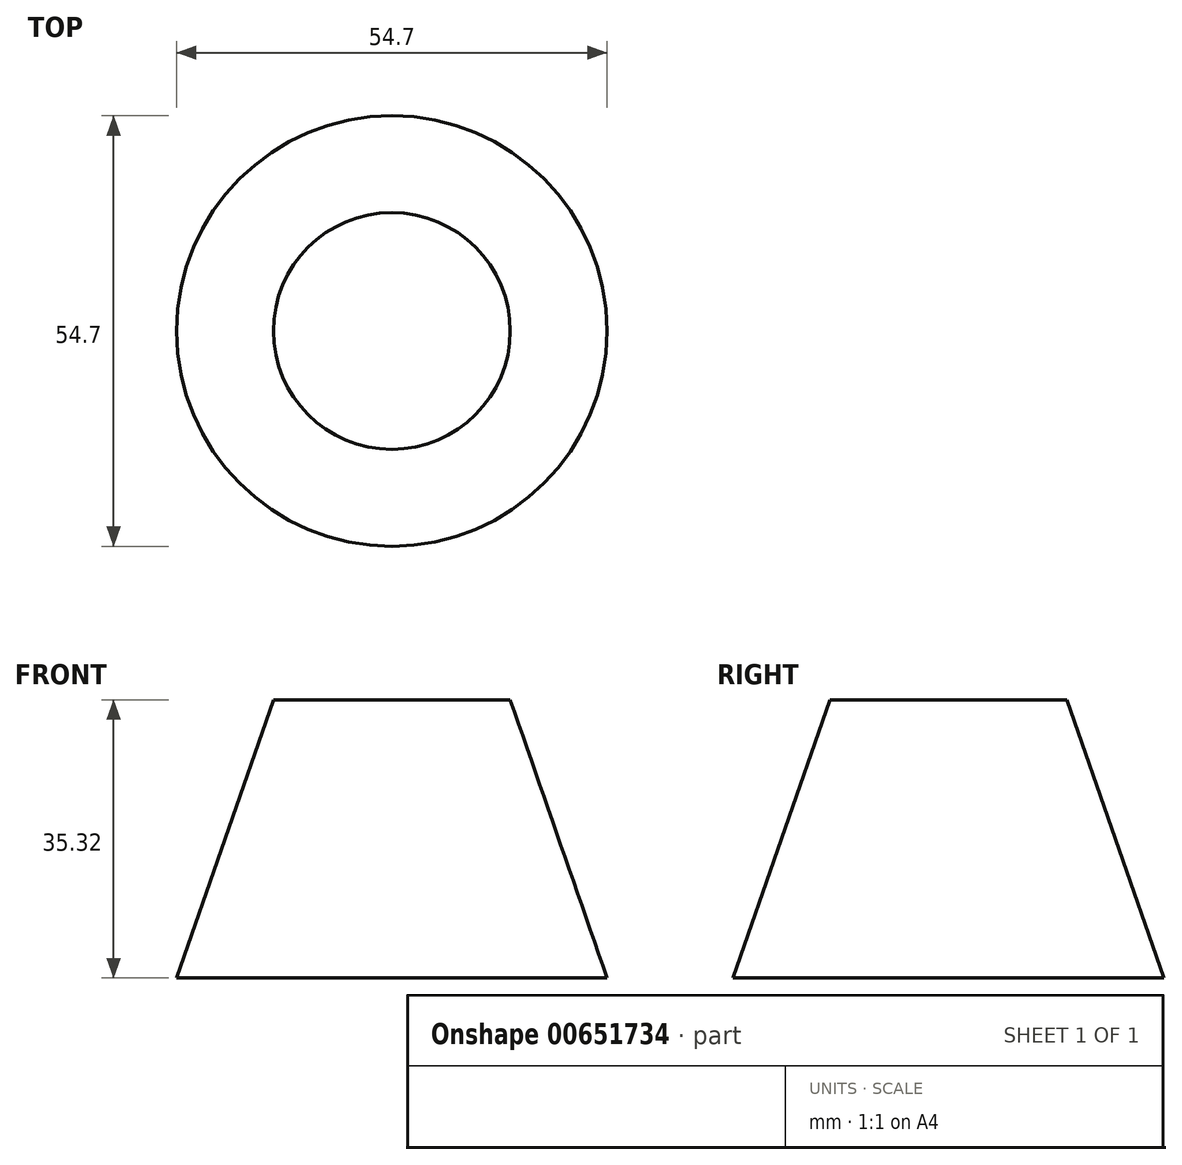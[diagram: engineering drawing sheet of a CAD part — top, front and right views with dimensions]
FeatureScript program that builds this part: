
annotation { "Feature Type Name" : "Feature", "Feature Type Description" : "" }
export const myFeature = defineFeature(function(context is Context, id is Id, definition is map)
    precondition{}
    {
        {
            var Q0;
            Q0=qCreatedBy(makeId("Front.planeOp"),FACE);
            var sketch = newSketch(context, id + "F0", { "sketchPlane" : qUnion([Q0])});
            skLineSegment(sketch, "E0", {"start": v(0, 0) * mm, "end": v(-27.35, 0) * mm});
            skLineSegment(sketch, "E1", {"start": v(-27.35, 0) * mm, "end": v(-15.04, 35.32) * mm});
            skLineSegment(sketch, "E2", {"start": v(-15.04, 35.32) * mm, "end": v(0, 35.32) * mm});
            skLineSegment(sketch, "E3", {"start": v(0, 35.32) * mm, "end": v(0, 0) * mm});
            skSolve(sketch);
        }
        {
            var Q0;
            Q0=qCreatedBy(makeId("Front.planeOp"),FACE);
            var sketch = newSketch(context, id + "F1", { "sketchPlane" : qUnion([Q0])});
            skLineSegment(sketch, "E4", {"start": v(0, 61.62) * mm, "end": v(0, -38.82) * mm, "construction": true});
            skSolve(sketch);
        }
        {
            var Q0;
            Q0=makeQuery(id+"F0.imprint","IMPRINT",FACE,{"disambiguationData":[TD([[makeQuery(id+"F0.imprint","IMPRINT",EDGE,{"derivedFrom":sQuery(id+"F0.wireOp",EDGE,"E0")}),-1.0]])]});
            var Q1;
            Q1=sQuery(id+"F1.wireOp",EDGE,"E4");
            revolve(context, id + "F2", {"entities" : qUnion([Q0]), "axis" : qUnion([Q1]), "revolveType" : RevolveType.FULL});
        }
    });
